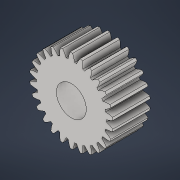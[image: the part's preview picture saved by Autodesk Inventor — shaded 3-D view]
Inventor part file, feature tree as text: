
AUTODESK INVENTOR PART (.ipt)
format: ipt  version: 2021 (Build 250183000, 183)  size: 309,760 bytes
history: native  units: mm (DEFAULTED — no unit token found)
features: plane x3, other x3, sketch x3, extrude x2
ambient origin geometry x8: Origin, YZ Plane, XZ Plane, XY Plane, X Axis, Y Axis, Z Axis, Center Point
bodies: Solid1 (feature_tree)
feature tree (11):
  extrude  "Extrusion1"  Depth=1.25mm TaperAngle=0.0deg
  plane  "Work Plane2"
  plane  "Work Plane8"
  plane  "Work Plane9"
  other  "Engrenagem reta"
  extrude  "Extrusão2"  Depth=10.0mm TaperAngle=0.0deg
  sketch  "Sketch1"  dims[d0=2.8mm d1=1.25mm d2=0.0mm]
  sketch  "Sketch2"  dims[d3=2.6mm d4=10.0mm d5=0.0mm]
  other  "Srf1"
  sketch  "Esboço3"  dims[d16=3.0mm d17=0.0mm d34=1.208305mm d39=0.0mm d41=0.0mm d43=3.0mm d46=3.0mm d47=0.0mm d48=0.0mm d49=1.0mm d50=1.5mm d51=0.0mm]
  other  "Diâmetro do flanco"
